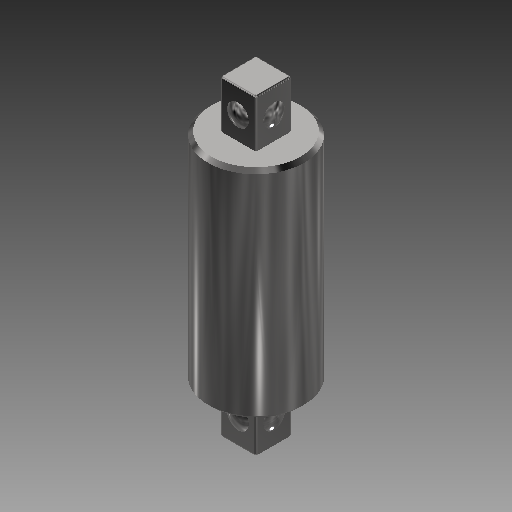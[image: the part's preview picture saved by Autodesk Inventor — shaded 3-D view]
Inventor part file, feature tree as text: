
AUTODESK INVENTOR PART (.ipt)
format: ipt  version: 2019 (Build 230136000, 136)  size: 190,464 bytes
history: native  units: mm
features: sketch x3, extrude x2, fillet x1, revolve x1, mirror x1, chamfer x1, plane x1, split x1, projected_geometry x1
ambient origin geometry x8: Origin, YZ Plane, XZ Plane, XY Plane, X Axis, Y Axis, Z Axis, Center Point
bodies: Solid1 (feature_tree)
feature tree (12):
  extrude  "Extrusion1"  Depth=18.0mm TaperAngle=0.0deg
  extrude  "Extrusion2"  Depth=3.0mm
  fillet  "Fillet1"  Radius=1.5mm
  revolve  "Revolution1"  [1 undecoded]
  mirror  "Mirror1"
  chamfer  "Chamfer2"  Distance=0.2mm
  plane  "Work Plane2"
  split  "Split2"
  sketch  "Sketch1"  dims[d0=8.0mm d1=18.0mm d2=0.0mm]
  sketch  "Sketch2"  dims[d3=3.0mm d4=3.0mm d5=1.5mm]
  sketch  "Sketch3"  dims[d6=1.5mm d7=4.0mm d8=0.0mm d9=0.2mm d10=1.75mm d11=3.5mm d12=90.0deg d16=0.3mm d17=2.0mm d18=45.0deg d20=-12.561708mm]
  projected_geometry  "Project Cut Edges1"
note: 1 required parameter value undecoded (feature->parameter linkage not recoverable at this tier; creation-order binding heuristic only, values carry confidence <= 0.55)
